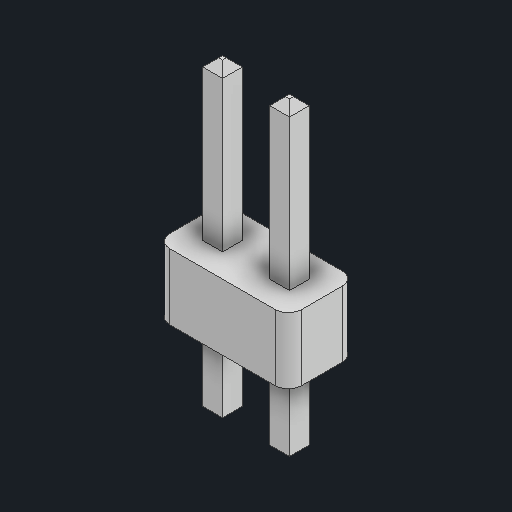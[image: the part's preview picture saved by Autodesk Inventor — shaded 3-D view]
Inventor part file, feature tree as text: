
AUTODESK INVENTOR PART (.ipt)
format: ipt  version: 2023 (Build 270158000, 158)  size: 106,496 bytes
history: native  units: in
note: dims shown in document units (in); Inventor stores cm internally (conversion verified against a paired STEP export)
features: chamfer x1
ambient origin geometry x8: Origin, YZ Plane, XZ Plane, XY Plane, X Axis, Y Axis, Z Axis, Center Point
bodies: Solid1 (feature_tree)
feature tree (1):
  chamfer  "Chamfer1"  [1 undecoded]
note: 1 required parameter value undecoded (feature->parameter linkage not recoverable at this tier; creation-order binding heuristic only, values carry confidence <= 0.55)
